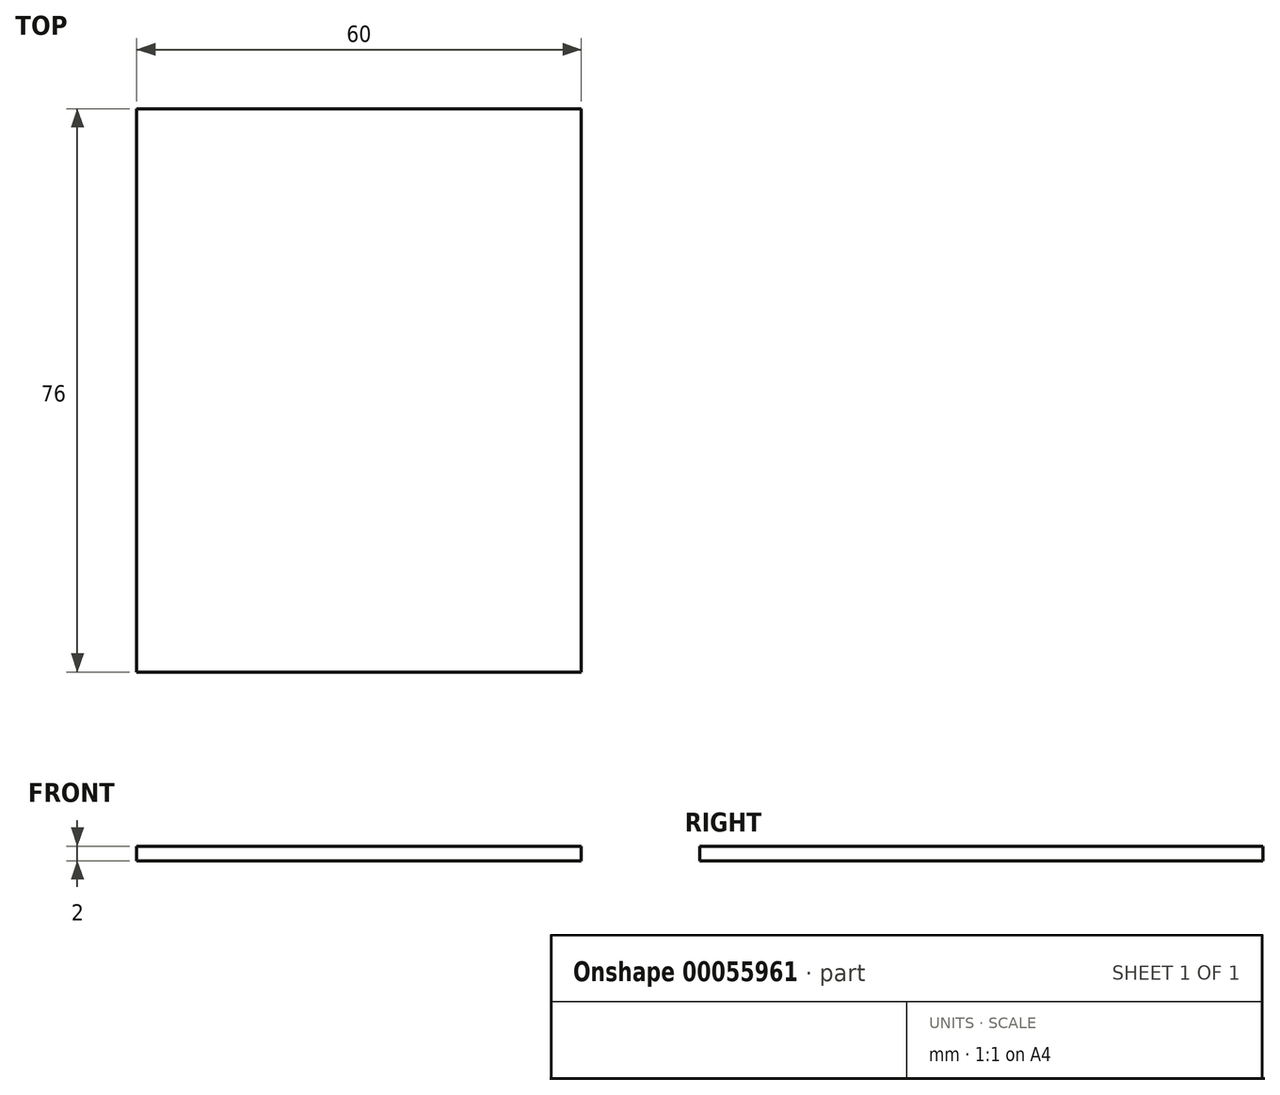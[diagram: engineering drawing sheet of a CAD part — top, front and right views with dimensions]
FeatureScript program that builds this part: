
annotation { "Feature Type Name" : "Feature", "Feature Type Description" : "" }
export const myFeature = defineFeature(function(context is Context, id is Id, definition is map)
    precondition{}
    {
        {
            var Q0;
            Q0=qCreatedBy(makeId("Top.planeOp"),FACE);
            var sketch = newSketch(context, id + "F0", { "sketchPlane" : qUnion([Q0])});
            skLineSegment(sketch, "E0.rect.bottom", {"start": v(30, 38) * mm, "end": v(-30, 38) * mm});
            skLineSegment(sketch, "E0.rect.top", {"start": v(30, -38) * mm, "end": v(-30, -38) * mm});
            skLineSegment(sketch, "E0.rect.left", {"start": v(30, 38) * mm, "end": v(30, -38) * mm});
            skLineSegment(sketch, "E0.rect.right", {"start": v(-30, 38) * mm, "end": v(-30, -38) * mm});
            skPoint(sketch, "E0.rect.middle", {"position": v(0, 0) * mm});
            skSolve(sketch);
        }
        {
            var Q0;
            Q0=makeQuery(id+"F0.imprint","IMPRINT",FACE,{"disambiguationData":[TD([[makeQuery(id+"F0.imprint","IMPRINT",EDGE,{"derivedFrom":sQuery(id+"F0.wireOp",EDGE,"E0.rect.bottom")}),1.0]])]});
            extrude(context, id + "F1", {"entities" : qUnion([Q0]), "depth" : 2 * mm});
        }
    });
